# Revit family: Screen_Window_PrestigeSeries_PhantomScreens-1
name_source: partatom
category: Windows
units: mm (PartAtom-declared; Revit-internal decimal feet)

## family parameters
Always vertical = Yes
Classification Number = 23.30.60.21
Cut with Voids When Loaded = No
Host = Wall
Room Calculation Point = No
Shared = No

## types (1)
- Type as Specified
    Aluminum Housing = Dark Ash
    Aluminum Slide Bar = Dark Ash
    Aluminum Track = Dark Ash
    Assembly Code = B2020400
    Construction Details = http://www.arcat.com
    Default Sill Height = 36 "
    Description = Phantom Screens Prestige Series Screen
    Housing Depth = 1.901 "
    Housing Height = 2.264 "
    Installation-Fabrication = http://www.phantomscreens.com
    Keynote = 08 11 00
    Manufacturer = Phantom Screens
    Manufacturer Fax = 604-855-7834
    Manufacturer Website = http://www.phantomscreens.com
    Model = Prestige Series
    Product Data = http://www.arcat.com
    Product Properties = http://www.phantomscreens.com
    Revision = R1_08-2016
    Sales Information = http://www.phantomscreens.com
    Screen = BetterVue™ Mesh
    Screen Thickness = 0.031 "
    Slide Bar Depth = 1.5 "
    Slide Bar Height = 1.395 "
    Specification = http://www.phantomscreens.com
    Track Depth = 0.871 "
    Track Width = 1.348 "
    URL = http://www.phantomscreens.com
    Wall Closure = By host
    Wooden Slide Bar = Dark Ash

## geometry (parser evidence)
native form markers: Sweep x3
no freeform markers — native parametric forms only
